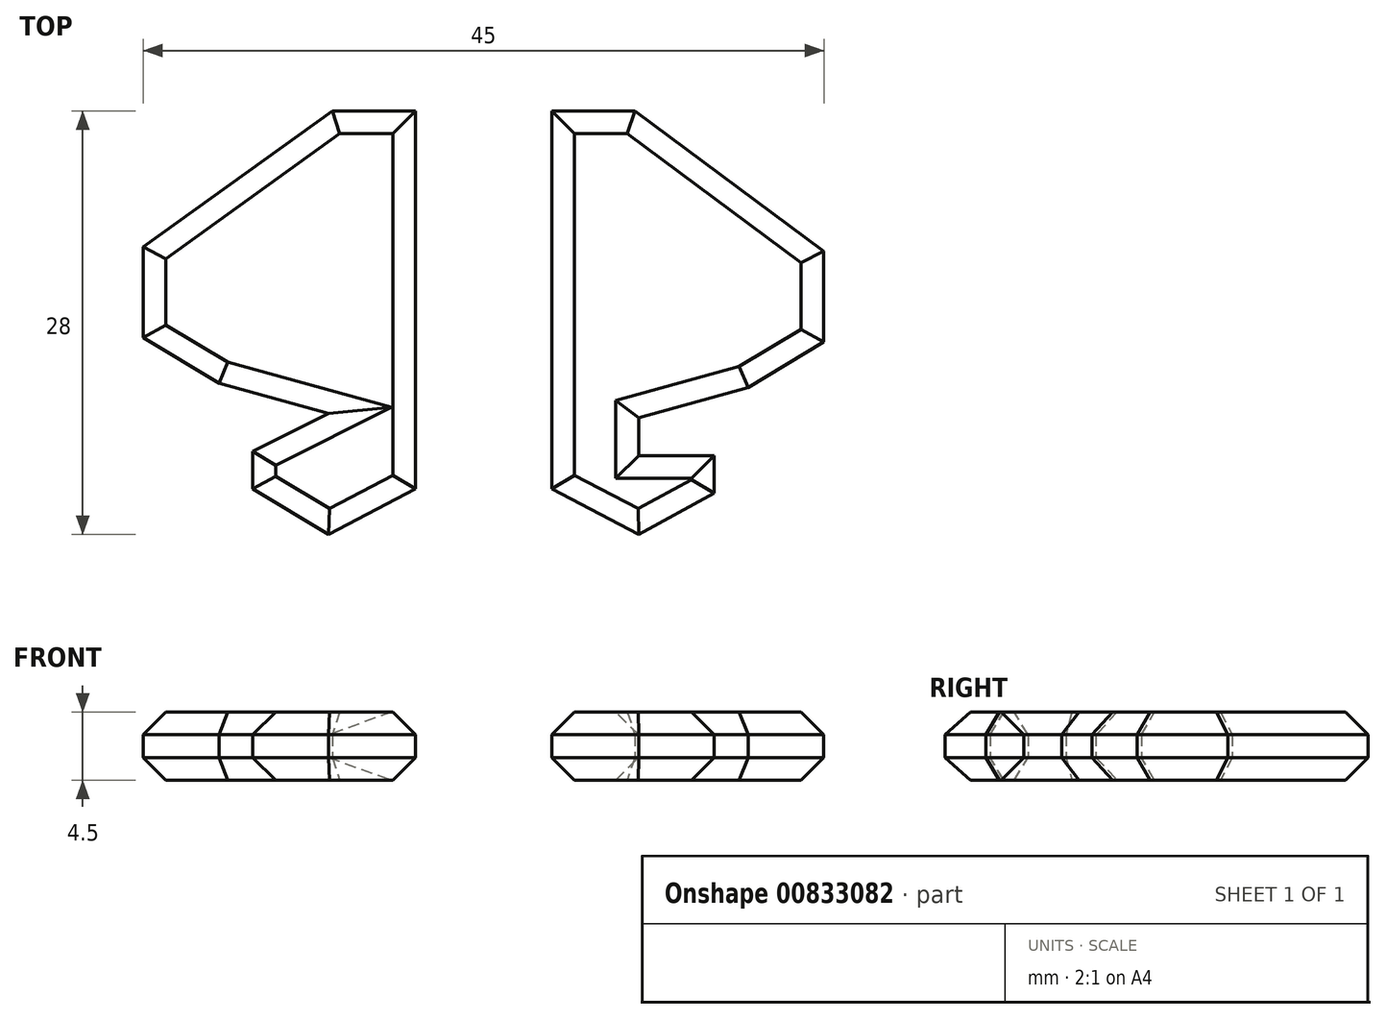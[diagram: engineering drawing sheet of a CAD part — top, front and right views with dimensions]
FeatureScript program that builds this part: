
annotation { "Feature Type Name" : "Feature", "Feature Type Description" : "" }
export const myFeature = defineFeature(function(context is Context, id is Id, definition is map)
    precondition{}
    {
        {
            var Q0;
            Q0=qCreatedBy(makeId("Top.planeOp"),FACE);
            var sketch = newSketch(context, id + "F0", { "sketchPlane" : qUnion([Q0])});
            skLineSegment(sketch, "E0.bottom", {"start": v(-28.2, 5.5) * mm, "end": v(16.8, 5.5) * mm});
            skLineSegment(sketch, "E0.top", {"start": v(-28.2, -57.5) * mm, "end": v(16.8, -57.5) * mm});
            skLineSegment(sketch, "E0.left", {"start": v(-28.2, 5.5) * mm, "end": v(-28.2, -57.5) * mm});
            skLineSegment(sketch, "E0.right", {"start": v(16.8, 5.5) * mm, "end": v(16.8, -57.5) * mm});
            skLineSegment(sketch, "E1", {"start": v(16.8, 5.5) * mm, "end": v(-0.7, 5.5) * mm});
            skLineSegment(sketch, "E2", {"start": v(-0.7, 5.5) * mm, "end": v(-0.7, -14.5) * mm});
            skLineSegment(sketch, "E3", {"start": v(4.3, -19.5) * mm, "end": v(-0.7, -14.5) * mm});
            skLineSegment(sketch, "E4", {"start": v(4.3, -19.5) * mm, "end": v(4.3, -29.5) * mm});
            skLineSegment(sketch, "E5", {"start": v(16.8, -29.8) * mm, "end": v(16.8, -38.8) * mm});
            skLineSegment(sketch, "E6", {"start": v(16.8, -38.8) * mm, "end": v(4.3, -29.5) * mm});
            skLineSegment(sketch, "E7", {"start": v(16.8, -38.8) * mm, "end": v(16.8, -44.8) * mm});
            skLineSegment(sketch, "E8", {"start": v(11.8, -47.8) * mm, "end": v(16.8, -44.8) * mm});
            skLineSegment(sketch, "E9", {"start": v(4.56, -49.8) * mm, "end": v(11.8, -47.8) * mm});
            skLineSegment(sketch, "E10", {"start": v(4.56, -49.8) * mm, "end": v(4.56, -52.3) * mm});
            skLineSegment(sketch, "E11", {"start": v(4.56, -52.3) * mm, "end": v(9.56, -52.3) * mm});
            skLineSegment(sketch, "E12", {"start": v(9.56, -52.3) * mm, "end": v(4.56, -49.8) * mm});
            skLineSegment(sketch, "E13", {"start": v(9.56, -52.3) * mm, "end": v(9.56, -54.8) * mm});
            skLineSegment(sketch, "E14", {"start": v(4.56, -57.5) * mm, "end": v(9.56, -54.8) * mm});
            skLineSegment(sketch, "E15", {"start": v(-1.2, -54.5) * mm, "end": v(4.56, -57.5) * mm});
            skLineSegment(sketch, "E16", {"start": v(-3.2, -54.5) * mm, "end": v(-5.2, -52) * mm});
            skLineSegment(sketch, "E17", {"start": v(-1.2, -52) * mm, "end": v(-3.2, -54.5) * mm});
            skLineSegment(sketch, "E18", {"start": v(-5.2, -52) * mm, "end": v(-5.2, -53.5) * mm});
            skLineSegment(sketch, "E19", {"start": v(-5.7, -54) * mm, "end": v(-6.2, -53.5) * mm});
            skLineSegment(sketch, "E20", {"start": v(-5.7, -54) * mm, "end": v(-5.2, -53.5) * mm});
            skLineSegment(sketch, "E21.MirrorCS", {"start": v(-20.94, -52) * mm, "end": v(-15.94, -49.5) * mm});
            skLineSegment(sketch, "E22.MirrorCS", {"start": v(-15.94, -49.5) * mm, "end": v(-23.2, -47.5) * mm});
            skLineSegment(sketch, "E23.MirrorCS", {"start": v(-20.94, -52) * mm, "end": v(-20.94, -54.5) * mm});
            skLineSegment(sketch, "E24.MirrorCS", {"start": v(-10.2, -54.5) * mm, "end": v(-15.94, -57.5) * mm});
            skLineSegment(sketch, "E25.MirrorCS", {"start": v(-15.94, -57.5) * mm, "end": v(-20.94, -54.5) * mm});
            skLineSegment(sketch, "E26.MirrorCS", {"start": v(-28.2, -38.5) * mm, "end": v(-28.2, -44.5) * mm});
            skLineSegment(sketch, "E27.MirrorCS", {"start": v(-23.2, -47.5) * mm, "end": v(-28.2, -44.5) * mm});
            skLineSegment(sketch, "E28.MirrorCS", {"start": v(-28.2, -29.5) * mm, "end": v(-28.2, -38.5) * mm});
            skLineSegment(sketch, "E29.MirrorCS", {"start": v(-15.7, -19.5) * mm, "end": v(-15.7, -29.5) * mm});
            skLineSegment(sketch, "E30.MirrorCS", {"start": v(-28.2, 5.5) * mm, "end": v(-10.7, 5.5) * mm});
            skLineSegment(sketch, "E31.MirrorCS", {"start": v(-28.2, -38.5) * mm, "end": v(-15.7, -29.5) * mm});
            skLineSegment(sketch, "E32.MirrorCS", {"start": v(-10.7, 5.5) * mm, "end": v(-10.7, -14.5) * mm});
            skLineSegment(sketch, "E33.MirrorCS", {"start": v(-15.7, -19.5) * mm, "end": v(-10.7, -14.5) * mm});
            skPoint(sketch, "E34.MirrorP", {"position": v(-5.7, -53.5) * mm});
            skLineSegment(sketch, "E35", {"start": v(-6.2, -53.5) * mm, "end": v(-6.2, -52) * mm});
            skLineSegment(sketch, "E36", {"start": v(-8.2, -54.5) * mm, "end": v(-6.2, -52) * mm});
            skLineSegment(sketch, "E37", {"start": v(-8.2, -54.5) * mm, "end": v(-10.2, -52) * mm});
            skLineSegment(sketch, "E38", {"start": v(-10.2, -54.5) * mm, "end": v(-10.2, -52) * mm});
            skLineSegment(sketch, "E39", {"start": v(-1.2, -54.5) * mm, "end": v(-1.2, -52) * mm});
            skLineSegment(sketch, "E40", {"start": v(-10.7, 5.5) * mm, "end": v(-5.7, 5.5) * mm});
            skLineSegment(sketch, "E41", {"start": v(-10.7, 5.5) * mm, "end": v(-10.7, -4.5) * mm});
            skArc(sketch, "E42", {"start": v(-5.7, 5.5) * mm, "mid": v(-9.42, -4.2) * mm, "end": v(-10.7, -14.5) * mm});
            skArc(sketch, "E43", {"start": v(-0.7, -14.5) * mm, "mid": v(-1.96, -4.2) * mm, "end": v(-5.7, 5.5) * mm});
            skArc(sketch, "E44.MirrorCS", {"start": v(-5.7, 5.5) * mm, "mid": v(-1.96, -4.2) * mm, "end": v(-0.7, -14.5) * mm});
            skArc(sketch, "E45.MirrorCS", {"start": v(-10.7, -14.5) * mm, "mid": v(-9.42, -4.2) * mm, "end": v(-5.7, 5.5) * mm});
            skPoint(sketch, "E46.endSnap0", {"position": v(-1.96, -4.2) * mm});
            skLineSegment(sketch, "E47", {"start": v(-0.7, -4.2) * mm, "end": v(-0.7, -16.7) * mm});
            skLineSegment(sketch, "E48", {"start": v(-10.7, -16.7) * mm, "end": v(-10.7, -4.5) * mm});
            skLineSegment(sketch, "E49", {"start": v(-10.7, -4.5) * mm, "end": v(-10.64, -12.4) * mm});
            skLineSegment(sketch, "E50", {"start": v(-10.7, -16.7) * mm, "end": v(-10.7, -10.6) * mm});
            skArc(sketch, "E51", {"start": v(-5.7, -16.7) * mm, "mid": v(-3.11, -10.53) * mm, "end": v(-5.7, -4.35) * mm});
            skArc(sketch, "E52", {"start": v(-5.7, -4.35) * mm, "mid": v(-8.27, -10.53) * mm, "end": v(-5.7, -16.7) * mm});
            skLineSegment(sketch, "E53", {"start": v(-15.7, -29.5) * mm, "end": v(4.3, -29.5) * mm});
            skLineSegment(sketch, "E54", {"start": v(-6.2, -52) * mm, "end": v(-6.2, -29.5) * mm});
            skLineSegment(sketch, "E55.bottom", {"start": v(-5.2, -52) * mm, "end": v(-6.2, -52) * mm});
            skLineSegment(sketch, "E55.top", {"start": v(-5.2, -29.5) * mm, "end": v(-6.2, -29.5) * mm});
            skLineSegment(sketch, "E55.left", {"start": v(-5.2, -52) * mm, "end": v(-5.2, -29.5) * mm});
            skLineSegment(sketch, "E56", {"start": v(-5.7, -54) * mm, "end": v(-5.7, 5.5) * mm});
            skLineSegment(sketch, "E57", {"start": v(-5.7, -29.5) * mm, "end": v(-5.7, -40.76) * mm});
            skPoint(sketch, "E57.endSnap0", {"position": v(-5.2, -40.76) * mm});
            skLineSegment(sketch, "E58.bottom", {"start": v(-10.2, -52) * mm, "end": v(-6.2, -52) * mm});
            skLineSegment(sketch, "E58.top", {"start": v(-10.2, -29.5) * mm, "end": v(-6.2, -29.5) * mm});
            skLineSegment(sketch, "E58.left", {"start": v(-10.2, -52) * mm, "end": v(-10.2, -29.5) * mm});
            skLineSegment(sketch, "E59.bottom", {"start": v(-5.2, -29.5) * mm, "end": v(-1.2, -29.5) * mm});
            skLineSegment(sketch, "E59.top", {"start": v(-5.2, -52) * mm, "end": v(-1.2, -52) * mm});
            skLineSegment(sketch, "E59.left", {"start": v(-5.2, -29.5) * mm, "end": v(-5.2, -52) * mm});
            skLineSegment(sketch, "E59.right", {"start": v(-1.2, -29.5) * mm, "end": v(-1.2, -52) * mm});
            skLineSegment(sketch, "E60.bottom", {"start": v(-0.7, -16.7) * mm, "end": v(-10.7, -16.7) * mm});
            skLineSegment(sketch, "E60.top", {"start": v(-0.7, 5.5) * mm, "end": v(-10.7, 5.5) * mm});
            skLineSegment(sketch, "E60.left", {"start": v(-0.7, -16.7) * mm, "end": v(-0.7, 5.5) * mm});
            skLineSegment(sketch, "E60.right", {"start": v(-10.7, -16.7) * mm, "end": v(-10.7, 5.5) * mm});
            skLineSegment(sketch, "E61.bottom", {"start": v(-10.7, -4.5) * mm, "end": v(-0.7, -4.5) * mm});
            skLineSegment(sketch, "E61.top", {"start": v(-10.7, 5.5) * mm, "end": v(-0.7, 5.5) * mm});
            skLineSegment(sketch, "E61.left", {"start": v(-10.7, -4.5) * mm, "end": v(-10.7, 5.5) * mm});
            skLineSegment(sketch, "E61.right", {"start": v(-0.7, -4.5) * mm, "end": v(-0.7, 5.5) * mm});
            skSolve(sketch);
        }
        {
            var Q0;
            {var subQ0=sQuery(id+"F0.wireOp",EDGE,"E6");Q0=makeQuery(id+"F0.imprint","IMPRINT",FACE,{"disambiguationData":[TD([[makeQuery(id+"F0.imprint","IMPRINT",EDGE,{"derivedFrom":subQ0}),1.0]])]});}
            extrude(context, id + "F1", {"entities" : qUnion([Q0]), "depth" : 4.5 * mm, "offsetDistance" : 25 * mm});
        }
        {
            var Q0;
            Q0=makeQuery(id+"F0.imprint","IMPRINT",FACE,{"disambiguationData":[TD([[makeQuery(id+"F0.imprint","IMPRINT",EDGE,{"derivedFrom":sQuery(id+"F0.wireOp",EDGE,"E21.MirrorCS")}),-1.0]])]});
            var Q1;
            {var subQ0=sQuery(id+"F0.wireOp",EDGE,"E6");Q1=makeQuery(id+"F0.imprint","IMPRINT",FACE,{"disambiguationData":[TD([[makeQuery(id+"F0.imprint","IMPRINT",EDGE,{"derivedFrom":subQ0}),1.0]])]});}
            extrude(context, id + "F2", {"entities" : qUnion([Q0, Q1]), "operationType" : NewBodyOperationType.ADD, "depth" : 4.5 * mm, "offsetDistance" : 25 * mm});
        }
        {
            var Q0;
            Q0=makeQuery(id+"F1.opExtrude","CAP_FACE",FACE,{"disambiguationData":[OSD([sQuery(id+"F0.wireOp",EDGE,"E6"),sQuery(id+"F0.wireOp",EDGE,"E7"),sQuery(id+"F0.wireOp",EDGE,"E8"),sQuery(id+"F0.wireOp",EDGE,"E9"),sQuery(id+"F0.wireOp",EDGE,"E10"),sQuery(id+"F0.wireOp",EDGE,"E11"),sQuery(id+"F0.wireOp",EDGE,"E13"),sQuery(id+"F0.wireOp",EDGE,"E14"),sQuery(id+"F0.wireOp",EDGE,"E15"),sQuery(id+"F0.wireOp",EDGE,"E39"),sQuery(id+"F0.wireOp",EDGE,"E53"),sQuery(id+"F0.wireOp",EDGE,"E59.right")])],"isStart":false});
            var Q1;
            Q1=makeQuery(id+"F1.opExtrude","CAP_FACE",FACE,{"disambiguationData":[OSD([sQuery(id+"F0.wireOp",EDGE,"E6"),sQuery(id+"F0.wireOp",EDGE,"E7"),sQuery(id+"F0.wireOp",EDGE,"E8"),sQuery(id+"F0.wireOp",EDGE,"E9"),sQuery(id+"F0.wireOp",EDGE,"E10"),sQuery(id+"F0.wireOp",EDGE,"E11"),sQuery(id+"F0.wireOp",EDGE,"E13"),sQuery(id+"F0.wireOp",EDGE,"E14"),sQuery(id+"F0.wireOp",EDGE,"E15"),sQuery(id+"F0.wireOp",EDGE,"E39"),sQuery(id+"F0.wireOp",EDGE,"E53"),sQuery(id+"F0.wireOp",EDGE,"E59.right")])],"isStart":true});
            var Q2;
            Q2=makeQuery(id+"F2.opExtrude","CAP_FACE",FACE,{"disambiguationData":[OSD([sQuery(id+"F0.wireOp",EDGE,"E21.MirrorCS"),sQuery(id+"F0.wireOp",EDGE,"E22.MirrorCS"),sQuery(id+"F0.wireOp",EDGE,"E23.MirrorCS"),sQuery(id+"F0.wireOp",EDGE,"E24.MirrorCS"),sQuery(id+"F0.wireOp",EDGE,"E25.MirrorCS"),sQuery(id+"F0.wireOp",EDGE,"E27.MirrorCS"),sQuery(id+"F0.wireOp",EDGE,"E31.MirrorCS"),sQuery(id+"F0.wireOp",EDGE,"E0.left"),sQuery(id+"F0.wireOp",EDGE,"E38"),sQuery(id+"F0.wireOp",EDGE,"E53"),sQuery(id+"F0.wireOp",EDGE,"E58.left")])],"isStart":false});
            var Q3;
            Q3=makeQuery(id+"F2.opExtrude","CAP_FACE",FACE,{"disambiguationData":[OSD([sQuery(id+"F0.wireOp",EDGE,"E21.MirrorCS"),sQuery(id+"F0.wireOp",EDGE,"E22.MirrorCS"),sQuery(id+"F0.wireOp",EDGE,"E23.MirrorCS"),sQuery(id+"F0.wireOp",EDGE,"E24.MirrorCS"),sQuery(id+"F0.wireOp",EDGE,"E25.MirrorCS"),sQuery(id+"F0.wireOp",EDGE,"E27.MirrorCS"),sQuery(id+"F0.wireOp",EDGE,"E31.MirrorCS"),sQuery(id+"F0.wireOp",EDGE,"E0.left"),sQuery(id+"F0.wireOp",EDGE,"E38"),sQuery(id+"F0.wireOp",EDGE,"E53"),sQuery(id+"F0.wireOp",EDGE,"E58.left")])],"isStart":true});
            var Q4;
            Q4=makeQuery(id+"F1.opExtrude","CAP_EDGE",EDGE,{"disambiguationData":[OSD([sQuery(id+"F0.wireOp",EDGE,"E53")])],"isStart":true});
            chamfer(context, id + "F3", {"entities" : qUnion([Q0, Q1, Q2, Q3, Q4]), "width" : 1.5 * mm, "tangentPropagation" : true});
        }
    });
